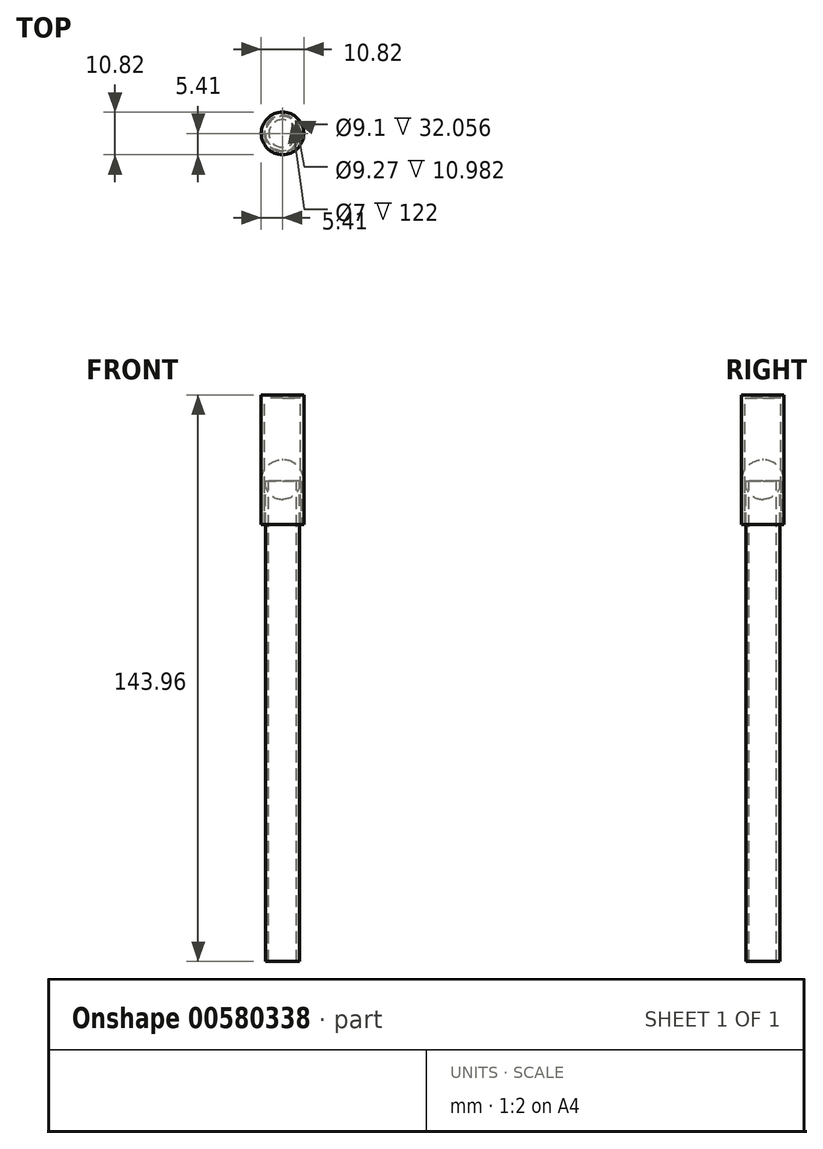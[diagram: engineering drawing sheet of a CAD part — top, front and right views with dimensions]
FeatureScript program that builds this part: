
annotation { "Feature Type Name" : "Feature", "Feature Type Description" : "" }
export const myFeature = defineFeature(function(context is Context, id is Id, definition is map)
    precondition{}
    {
        {
            var Q0;
            Q0=qCreatedBy(makeId("Front.planeOp"),FACE);
            var sketch = newSketch(context, id + "F0", { "sketchPlane" : qUnion([Q0])});
            skLineSegment(sketch, "E0", {"start": v(0, 0) * mm, "end": v(-3.5, 0) * mm});
            skLineSegment(sketch, "E1", {"start": v(-3.5, 0) * mm, "end": v(-3.5, -122) * mm});
            skLineSegment(sketch, "E2", {"start": v(-3.5, 0) * mm, "end": v(-4.35, 0) * mm});
            skLineSegment(sketch, "E3", {"start": v(-4.35, 0) * mm, "end": v(-4.35, -122) * mm});
            skLineSegment(sketch, "E4", {"start": v(-4.35, -122) * mm, "end": v(-3.5, -122) * mm});
            skLineSegment(sketch, "E5", {"start": v(0, 0) * mm, "end": v(0, -8.07) * mm});
            skLineSegment(sketch, "E6", {"start": v(-4.6, 0) * mm, "end": v(-4.6, -10.99) * mm});
            skLineSegment(sketch, "E7", {"start": v(-4.6, -10.99) * mm, "end": v(-5.44, -10.99) * mm});
            skLineSegment(sketch, "E8", {"start": v(-5.44, -10.99) * mm, "end": v(-5.44, 0) * mm});
            skLineSegment(sketch, "E9", {"start": v(-5.44, 0) * mm, "end": v(-4.6, 0) * mm});
            skLineSegment(sketch, "E10", {"start": v(0.01, 0) * mm, "end": v(-5.43, 0) * mm});
            skArc(sketch, "E11", {"start": v(0.01, 5.45) * mm, "mid": v(-3.84, 3.86) * mm, "end": v(-5.44, 0) * mm});
            skLineSegment(sketch, "E12", {"start": v(0, 4.63) * mm, "end": v(0, 0.03) * mm});
            skArc(sketch, "E13", {"start": v(0, 4.63) * mm, "mid": v(-3.25, 3.26) * mm, "end": v(-4.6, 0) * mm});
            skLineSegment(sketch, "E14", {"start": v(0.01, 5.45) * mm, "end": v(0, 4.63) * mm});
            skSolve(sketch);
        }
        {
            var Q0;
            Q0=makeQuery(id+"F0.imprint","IMPRINT",FACE,{"disambiguationData":[TD([[makeQuery(id+"F0.imprint","IMPRINT",EDGE,{"derivedFrom":sQuery(id+"F0.wireOp",EDGE,"E1")}),-1.0]])]});
            var Q1;
            Q1=sQuery(id+"F0.wireOp",EDGE,"E5");
            revolve(context, id + "F1", {"entities" : qUnion([Q0]), "axis" : qUnion([Q1]), "revolveType" : RevolveType.FULL});
        }
        {
            var Q0;
            Q0=qCreatedBy(makeId("Front.planeOp"),FACE);
            var sketch = newSketch(context, id + "F2", { "sketchPlane" : qUnion([Q0])});
            skLineSegment(sketch, "E15", {"start": v(-4.64, 0.04) * mm, "end": v(-4.64, -10.94) * mm});
            skLineSegment(sketch, "E16", {"start": v(-4.64, -10.94) * mm, "end": v(-5.4, -10.94) * mm});
            skLineSegment(sketch, "E17", {"start": v(-5.4, -10.94) * mm, "end": v(-5.4, 0.04) * mm});
            skArc(sketch, "E18", {"start": v(0, 5.5) * mm, "mid": v(-3.83, 3.88) * mm, "end": v(-5.4, 0.04) * mm});
            skArc(sketch, "E19", {"start": v(0, 4.67) * mm, "mid": v(-3.28, 3.31) * mm, "end": v(-4.64, 0.04) * mm});
            skLineSegment(sketch, "E20", {"start": v(0, 4.67) * mm, "end": v(0, 5.5) * mm});
            skLineSegment(sketch, "E21", {"start": v(0, 0) * mm, "end": v(0, 3.14) * mm});
            skSolve(sketch);
        }
        {
            var Q0;
            Q0=makeQuery(id+"F2.imprint","IMPRINT",FACE,{"disambiguationData":[TD([[makeQuery(id+"F2.imprint","IMPRINT",EDGE,{"derivedFrom":sQuery(id+"F2.wireOp",EDGE,"E15")}),-1.0]])]});
            var Q1;
            Q1=sQuery(id+"F2.wireOp",EDGE,"E21");
            revolve(context, id + "F3", {"entities" : qUnion([Q0]), "axis" : qUnion([Q1]), "revolveType" : RevolveType.FULL});
        }
        {
            var Q0;
            Q0=qCreatedBy(makeId("Front.planeOp"),FACE);
            var sketch = newSketch(context, id + "F4", { "sketchPlane" : qUnion([Q0])});
            skLineSegment(sketch, "E22", {"start": v(0, 32.08) * mm, "end": v(0, -34.7) * mm});
            skLineSegment(sketch, "E23", {"start": v(-4.55, -10.95) * mm, "end": v(-5.4, -10.95) * mm});
            skLineSegment(sketch, "E24", {"start": v(-4.55, 21.1) * mm, "end": v(0, 21.1) * mm});
            skLineSegment(sketch, "E25", {"start": v(0, 21.1) * mm, "end": v(0, 21.96) * mm});
            skLineSegment(sketch, "E26", {"start": v(0, 21.96) * mm, "end": v(-5.4, 21.96) * mm});
            skLineSegment(sketch, "E27", {"start": v(-5.4, -10.95) * mm, "end": v(-5.4, 21.96) * mm});
            skLineSegment(sketch, "E28", {"start": v(-4.55, 21.1) * mm, "end": v(-4.55, -10.95) * mm});
            skSolve(sketch);
        }
        {
            var Q0;
            Q0=makeQuery(id+"F4.imprint","IMPRINT",FACE,{"disambiguationData":[TD([[makeQuery(id+"F4.imprint","IMPRINT",EDGE,{"derivedFrom":sQuery(id+"F4.wireOp",EDGE,"E23")}),-1.0]])]});
            var Q1;
            Q1=sQuery(id+"F4.wireOp",EDGE,"E22");
            revolve(context, id + "F5", {"entities" : qUnion([Q0]), "axis" : qUnion([Q1]), "revolveType" : RevolveType.FULL});
        }
    });
